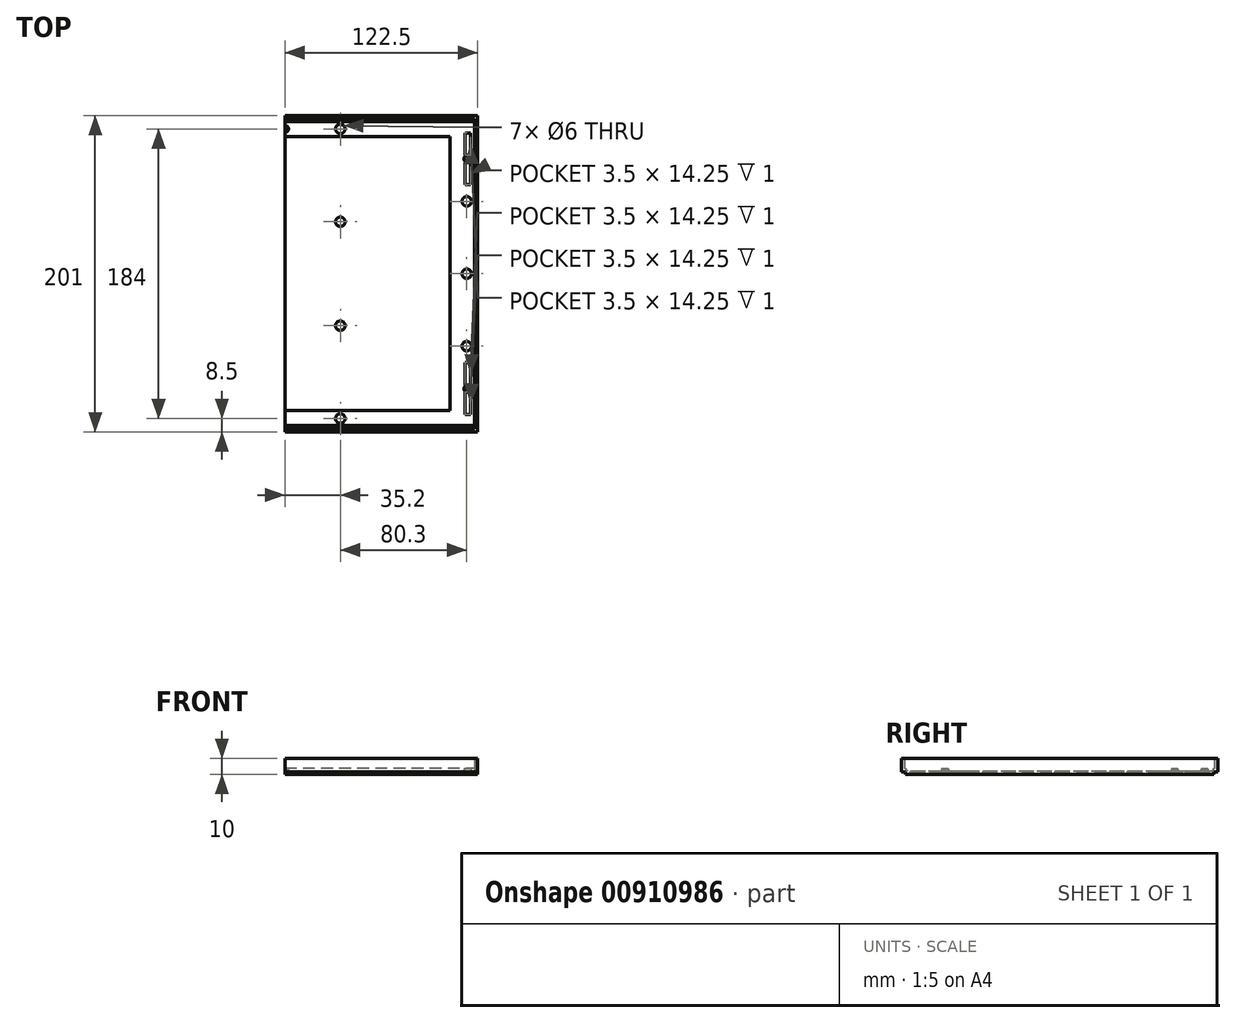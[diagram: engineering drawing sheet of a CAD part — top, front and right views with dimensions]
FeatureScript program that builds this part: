
annotation { "Feature Type Name" : "Feature", "Feature Type Description" : "" }
export const myFeature = defineFeature(function(context is Context, id is Id, definition is map)
    precondition{}
    {
        {
            var Q0;
            Q0=qCreatedBy(makeId("Top.planeOp"),FACE);
            var sketch = newSketch(context, id + "F0", { "sketchPlane" : qUnion([Q0])});
            skLineSegment(sketch, "E0.bottom", {"start": v(0, 0) * mm, "end": v(245, 0) * mm});
            skLineSegment(sketch, "E0.top", {"start": v(0, -201) * mm, "end": v(245, -201) * mm});
            skLineSegment(sketch, "E0.left", {"start": v(0, 0) * mm, "end": v(0, -201) * mm});
            skLineSegment(sketch, "E0.right", {"start": v(245, 0) * mm, "end": v(245, -201) * mm});
            skSolve(sketch);
        }
        {
            var Q0;
            Q0 = qSketchRegion(id + "F0", true);
            extrude(context, id + "F1", {"entities" : qUnion([Q0]), "depth" : 8 * mm, "offsetDistance" : 25 * mm});
        }
        {
            var Q0;
            Q0=makeQuery(id+"F1.opExtrude","CAP_FACE",FACE,{"disambiguationData":[OSD([sQuery(id+"F0.wireOp",EDGE,"E0.bottom"),sQuery(id+"F0.wireOp",EDGE,"E0.top"),sQuery(id+"F0.wireOp",EDGE,"E0.left"),sQuery(id+"F0.wireOp",EDGE,"E0.right")])],"isStart":false});
            shell(context, id + "F2", {"entities" : qUnion([Q0]), "thickness" : 2 * mm});
        }
        {
            var Q0;
            Q0=makeQuery(id+"F2.opShell","OFFSET_FACE",FACE,{"disambiguationData":[OSD([sQuery(id+"F0.wireOp",EDGE,"E0.bottom"),sQuery(id+"F0.wireOp",EDGE,"E0.top"),sQuery(id+"F0.wireOp",EDGE,"E0.left"),sQuery(id+"F0.wireOp",EDGE,"E0.right")])]});
            var sketch = newSketch(context, id + "F3", { "sketchPlane" : qUnion([Q0])});
            skLineSegment(sketch, "E1.bottom", {"start": v(17.5, -13.5) * mm, "end": v(227.5, -13.5) * mm});
            skLineSegment(sketch, "E1.top", {"start": v(17.5, -187.5) * mm, "end": v(227.5, -187.5) * mm});
            skLineSegment(sketch, "E1.left", {"start": v(17.5, -13.5) * mm, "end": v(17.5, -187.5) * mm});
            skLineSegment(sketch, "E1.right", {"start": v(227.5, -13.5) * mm, "end": v(227.5, -187.5) * mm});
            skSolve(sketch);
        }
        {
            var Q0;
            Q0 = qSketchRegion(id + "F3", true);
            extrude(context, id + "F4", {"entities" : qUnion([Q0]), "operationType" : NewBodyOperationType.REMOVE, "oppositeDirection" : true, "depth" : 1 * mm, "offsetDistance" : 25 * mm});
        }
        {
            var Q0;
            Q0=makeQuery(id+"F2.opShell","OFFSET_FACE",FACE,{"disambiguationData":[OSD([sQuery(id+"F0.wireOp",EDGE,"E0.bottom"),sQuery(id+"F0.wireOp",EDGE,"E0.top"),sQuery(id+"F0.wireOp",EDGE,"E0.left"),sQuery(id+"F0.wireOp",EDGE,"E0.right")])]});
            var sketch = newSketch(context, id + "F5", { "sketchPlane" : qUnion([Q0])});
            skLineSegment(sketch, "E2.bottom", {"start": v(4.5, -11) * mm, "end": v(8, -11) * mm});
            skLineSegment(sketch, "E2.top", {"start": v(4.5, -44) * mm, "end": v(8, -44) * mm});
            skLineSegment(sketch, "E2.left", {"start": v(4.5, -11) * mm, "end": v(4.5, -44) * mm});
            skLineSegment(sketch, "E2.right", {"start": v(8, -11) * mm, "end": v(8, -44) * mm});
            skLineSegment(sketch, "E3.bottom", {"start": v(4.5, -157) * mm, "end": v(8, -157) * mm});
            skLineSegment(sketch, "E3.top", {"start": v(4.5, -190) * mm, "end": v(8, -190) * mm});
            skLineSegment(sketch, "E3.left", {"start": v(4.5, -157) * mm, "end": v(4.5, -190) * mm});
            skLineSegment(sketch, "E3.right", {"start": v(8, -157) * mm, "end": v(8, -190) * mm});
            skLineSegment(sketch, "E4.bottom", {"start": v(237, -11) * mm, "end": v(240.5, -11) * mm});
            skLineSegment(sketch, "E4.top", {"start": v(237, -44) * mm, "end": v(240.5, -44) * mm});
            skLineSegment(sketch, "E4.left", {"start": v(237, -11) * mm, "end": v(237, -44) * mm});
            skLineSegment(sketch, "E4.right", {"start": v(240.5, -11) * mm, "end": v(240.5, -44) * mm});
            skLineSegment(sketch, "E5.bottom", {"start": v(237, -157) * mm, "end": v(240.5, -157) * mm});
            skLineSegment(sketch, "E5.top", {"start": v(237, -190) * mm, "end": v(240.5, -190) * mm});
            skLineSegment(sketch, "E5.left", {"start": v(237, -157) * mm, "end": v(237, -190) * mm});
            skLineSegment(sketch, "E5.right", {"start": v(240.5, -157) * mm, "end": v(240.5, -190) * mm});
            skSolve(sketch);
        }
        {
            var Q0;
            Q0 = qSketchRegion(id + "F5", true);
            extrude(context, id + "F6", {"entities" : qUnion([Q0]), "operationType" : NewBodyOperationType.REMOVE, "oppositeDirection" : true, "depth" : 1 * mm, "offsetDistance" : 25 * mm});
        }
        {
            var Q0;
            Q0=makeQuery(id+"F2.opShell","OFFSET_FACE",FACE,{"disambiguationData":[OSD([sQuery(id+"F0.wireOp",EDGE,"E0.bottom"),sQuery(id+"F0.wireOp",EDGE,"E0.top"),sQuery(id+"F0.wireOp",EDGE,"E0.left"),sQuery(id+"F0.wireOp",EDGE,"E0.right")])]});
            var sketch = newSketch(context, id + "F7", { "sketchPlane" : qUnion([Q0])});
            skCircle(sketch, "E6", {"center": v(238, -7) * mm, "radius": 2.75 * mm});
            skCircle(sketch, "E7", {"center": v(7, -7) * mm, "radius": 2.75 * mm});
            skCircle(sketch, "E8", {"center": v(7, -194) * mm, "radius": 2.75 * mm});
            skCircle(sketch, "E9", {"center": v(238, -194) * mm, "radius": 2.75 * mm});
            skSolve(sketch);
        }
        {
            var Q0;
            Q0=makeQuery(id+"F2.opShell","OFFSET_FACE",FACE,{"disambiguationData":[OSD([sQuery(id+"F0.wireOp",EDGE,"E0.bottom"),sQuery(id+"F0.wireOp",EDGE,"E0.top"),sQuery(id+"F0.wireOp",EDGE,"E0.left"),sQuery(id+"F0.wireOp",EDGE,"E0.right")])]});
            var sketch = newSketch(context, id + "F8", { "sketchPlane" : qUnion([Q0])});
            skLineSegment(sketch, "E10", {"start": v(237, -175.75) * mm, "end": v(240.5, -175.75) * mm});
            skLineSegment(sketch, "E11", {"start": v(240.5, -175.75) * mm, "end": v(240.5, -171.25) * mm});
            skLineSegment(sketch, "E12", {"start": v(240.5, -171.25) * mm, "end": v(237, -171.25) * mm});
            skLineSegment(sketch, "E13", {"start": v(237, -175.75) * mm, "end": v(237, -171.25) * mm});
            skLineSegment(sketch, "E14.bottom", {"start": v(240.5, -25.25) * mm, "end": v(237, -25.25) * mm});
            skLineSegment(sketch, "E14.top", {"start": v(240.5, -29.75) * mm, "end": v(237, -29.75) * mm});
            skLineSegment(sketch, "E14.left", {"start": v(240.5, -25.25) * mm, "end": v(240.5, -29.75) * mm});
            skLineSegment(sketch, "E14.right", {"start": v(237, -25.25) * mm, "end": v(237, -29.75) * mm});
            skLineSegment(sketch, "E15.bottom", {"start": v(8, -25.25) * mm, "end": v(4.5, -25.25) * mm});
            skLineSegment(sketch, "E15.top", {"start": v(8, -29.75) * mm, "end": v(4.5, -29.75) * mm});
            skLineSegment(sketch, "E15.left", {"start": v(8, -25.25) * mm, "end": v(8, -29.75) * mm});
            skLineSegment(sketch, "E15.right", {"start": v(4.5, -25.25) * mm, "end": v(4.5, -29.75) * mm});
            skLineSegment(sketch, "E16.bottom", {"start": v(8, -175.75) * mm, "end": v(4.5, -175.75) * mm});
            skLineSegment(sketch, "E16.top", {"start": v(8, -171.25) * mm, "end": v(4.5, -171.25) * mm});
            skLineSegment(sketch, "E16.left", {"start": v(8, -175.75) * mm, "end": v(8, -171.25) * mm});
            skLineSegment(sketch, "E16.right", {"start": v(4.5, -175.75) * mm, "end": v(4.5, -171.25) * mm});
            skSolve(sketch);
        }
        {
            var Q0;
            Q0 = qSketchRegion(id + "F8", true);
            extrude(context, id + "F9", {"entities" : qUnion([Q0]), "operationType" : NewBodyOperationType.ADD, "oppositeDirection" : true, "depth" : 1 * mm, "offsetDistance" : 25 * mm});
        }
        {
            var Q0;
            Q0=makeQuery(id+"F9.boolean.opBoolean","MERGE",FACE,{"derivedFrom":[makeQuery(id+"F2.opShell","OFFSET_FACE",FACE,{"disambiguationData":[OSD([sQuery(id+"F0.wireOp",EDGE,"E0.bottom"),sQuery(id+"F0.wireOp",EDGE,"E0.top"),sQuery(id+"F0.wireOp",EDGE,"E0.left"),sQuery(id+"F0.wireOp",EDGE,"E0.right")])]}),makeQuery(id+"F9.opExtrude","CAP_FACE",FACE,{"disambiguationData":[OSD([sQuery(id+"F8.wireOp",EDGE,"E10"),sQuery(id+"F8.wireOp",EDGE,"E11"),sQuery(id+"F8.wireOp",EDGE,"E12"),sQuery(id+"F8.wireOp",EDGE,"E13")])],"isStart":true}),makeQuery(id+"F9.opExtrude","CAP_FACE",FACE,{"disambiguationData":[OSD([sQuery(id+"F8.wireOp",EDGE,"E14.bottom"),sQuery(id+"F8.wireOp",EDGE,"E14.top"),sQuery(id+"F8.wireOp",EDGE,"E14.left"),sQuery(id+"F8.wireOp",EDGE,"E14.right")])],"isStart":true}),makeQuery(id+"F9.opExtrude","CAP_FACE",FACE,{"disambiguationData":[OSD([sQuery(id+"F8.wireOp",EDGE,"E15.bottom"),sQuery(id+"F8.wireOp",EDGE,"E15.top"),sQuery(id+"F8.wireOp",EDGE,"E15.left"),sQuery(id+"F8.wireOp",EDGE,"E15.right")])],"isStart":true}),makeQuery(id+"F9.opExtrude","CAP_FACE",FACE,{"disambiguationData":[OSD([sQuery(id+"F8.wireOp",EDGE,"E16.bottom"),sQuery(id+"F8.wireOp",EDGE,"E16.top"),sQuery(id+"F8.wireOp",EDGE,"E16.left"),sQuery(id+"F8.wireOp",EDGE,"E16.right")])],"isStart":true})]});
            var sketch = newSketch(context, id + "F10", { "sketchPlane" : qUnion([Q0])});
            skCircle(sketch, "E17", {"center": v(238.5, -27.5) * mm, "radius": 2.25 * mm});
            skCircle(sketch, "E18", {"center": v(6.5, -27.5) * mm, "radius": 2.25 * mm});
            skCircle(sketch, "E19", {"center": v(6.5, -173.5) * mm, "radius": 2.25 * mm});
            skCircle(sketch, "E20", {"center": v(238.5, -173.5) * mm, "radius": 2.25 * mm});
            skCircle(sketch, "E21", {"center": v(122.5, -8.5) * mm, "radius": 2.25 * mm});
            skSolve(sketch);
        }
        {
            var Q0;
            Q0 = qSketchRegion(id + "F10", true);
            extrude(context, id + "F11", {"entities" : qUnion([Q0]), "operationType" : NewBodyOperationType.ADD, "depth" : 1.5 * mm, "offsetDistance" : 25 * mm});
        }
        {
            var Q0;
            Q0=makeQuery(id+"F11.opExtrude","CAP_EDGE",EDGE,{"disambiguationData":[OSD([sQuery(id+"F10.wireOp",EDGE,"E20")])],"isStart":false});
            var Q1;
            Q1=makeQuery(id+"F11.opExtrude","CAP_EDGE",EDGE,{"disambiguationData":[OSD([sQuery(id+"F10.wireOp",EDGE,"E19")])],"isStart":false});
            var Q2;
            Q2=makeQuery(id+"F11.opExtrude","CAP_EDGE",EDGE,{"disambiguationData":[OSD([sQuery(id+"F10.wireOp",EDGE,"E17")])],"isStart":false});
            var Q3;
            Q3=makeQuery(id+"F11.opExtrude","CAP_EDGE",EDGE,{"disambiguationData":[OSD([sQuery(id+"F10.wireOp",EDGE,"E18")])],"isStart":false});
            var Q4;
            Q4=makeQuery(id+"F11.opExtrude","CAP_EDGE",EDGE,{"disambiguationData":[OSD([sQuery(id+"F10.wireOp",EDGE,"E21")])],"isStart":false});
            chamfer(context, id + "F12", {"entities" : qUnion([Q0, Q1, Q2, Q3, Q4]), "chamferType" : ChamferType.OFFSET_ANGLE, "width" : .15 * mm, "oppositeDirection" : false, "angle" : 84.25 * degree, "tangentPropagation" : true});
        }
        {
            var Q0;
            Q0=makeQuery(id+"F9.boolean.opBoolean","MERGE",FACE,{"derivedFrom":[makeQuery(id+"F2.opShell","OFFSET_FACE",FACE,{"disambiguationData":[OSD([sQuery(id+"F0.wireOp",EDGE,"E0.bottom"),sQuery(id+"F0.wireOp",EDGE,"E0.top"),sQuery(id+"F0.wireOp",EDGE,"E0.left"),sQuery(id+"F0.wireOp",EDGE,"E0.right")])]}),makeQuery(id+"F9.opExtrude","CAP_FACE",FACE,{"disambiguationData":[OSD([sQuery(id+"F8.wireOp",EDGE,"E10"),sQuery(id+"F8.wireOp",EDGE,"E11"),sQuery(id+"F8.wireOp",EDGE,"E12"),sQuery(id+"F8.wireOp",EDGE,"E13")])],"isStart":true}),makeQuery(id+"F9.opExtrude","CAP_FACE",FACE,{"disambiguationData":[OSD([sQuery(id+"F8.wireOp",EDGE,"E14.bottom"),sQuery(id+"F8.wireOp",EDGE,"E14.top"),sQuery(id+"F8.wireOp",EDGE,"E14.left"),sQuery(id+"F8.wireOp",EDGE,"E14.right")])],"isStart":true}),makeQuery(id+"F9.opExtrude","CAP_FACE",FACE,{"disambiguationData":[OSD([sQuery(id+"F8.wireOp",EDGE,"E15.bottom"),sQuery(id+"F8.wireOp",EDGE,"E15.top"),sQuery(id+"F8.wireOp",EDGE,"E15.left"),sQuery(id+"F8.wireOp",EDGE,"E15.right")])],"isStart":true}),makeQuery(id+"F9.opExtrude","CAP_FACE",FACE,{"disambiguationData":[OSD([sQuery(id+"F8.wireOp",EDGE,"E16.bottom"),sQuery(id+"F8.wireOp",EDGE,"E16.top"),sQuery(id+"F8.wireOp",EDGE,"E16.left"),sQuery(id+"F8.wireOp",EDGE,"E16.right")])],"isStart":true})]});
            var sketch = newSketch(context, id + "F13", { "sketchPlane" : qUnion([Q0])});
            skCircle(sketch, "E22", {"center": v(7, -54.5) * mm, "radius": 3 * mm});
            skCircle(sketch, "E23", {"center": v(7, -100.5) * mm, "radius": 3 * mm});
            skCircle(sketch, "E24", {"center": v(7, -146.5) * mm, "radius": 3 * mm});
            skCircle(sketch, "E25.MirrorC", {"center": v(238, -54.5) * mm, "radius": 3 * mm});
            skCircle(sketch, "E26.MirrorC", {"center": v(238, -100.5) * mm, "radius": 3 * mm});
            skCircle(sketch, "E27.MirrorC", {"center": v(238, -146.5) * mm, "radius": 3 * mm});
            skCircle(sketch, "E28", {"center": v(87.3, -8.5) * mm, "radius": 3 * mm});
            skCircle(sketch, "E29", {"center": v(87.3, -67.5) * mm, "radius": 3 * mm});
            skPoint(sketch, "E30.0", {"position": v(122.5, -12.5) * mm});
            skPoint(sketch, "E31.MirrorP", {"position": v(122.5, -364.5) * mm});
            skPoint(sketch, "E32.MirrorP", {"position": v(122.5, -188.5) * mm});
            skCircle(sketch, "E33.MirrorC", {"center": v(157.7, -8.5) * mm, "radius": 3 * mm});
            skCircle(sketch, "E34.MirrorC", {"center": v(157.7, -67.5) * mm, "radius": 3 * mm});
            skCircle(sketch, "E35.MirrorC", {"center": v(157.7, -133.5) * mm, "radius": 3 * mm});
            skCircle(sketch, "E36.MirrorC", {"center": v(157.7, -192.5) * mm, "radius": 3 * mm});
            skCircle(sketch, "E37.MirrorC", {"center": v(87.3, -192.5) * mm, "radius": 3 * mm});
            skCircle(sketch, "E38.MirrorC", {"center": v(87.3, -133.5) * mm, "radius": 3 * mm});
            skSolve(sketch);
        }
        {
            var Q0;
            Q0 = qSketchRegion(id + "F13", true);
            extrude(context, id + "F14", {"entities" : qUnion([Q0]), "operationType" : NewBodyOperationType.REMOVE, "endBound" : BoundingType.THROUGH_ALL, "oppositeDirection" : true, "depth" : 25 * mm, "offsetDistance" : 25 * mm});
        }
        {
            var Q0;
            Q0=makeQuery(id+"F1.opExtrude","SWEPT_FACE",FACE,{"disambiguationData":[OSD([sQuery(id+"F0.wireOp",EDGE,"E0.left")])]});
            var sketch = newSketch(context, id + "F15", { "sketchPlane" : qUnion([Q0])});
            skLineSegment(sketch, "E39.bottom", {"start": v(2.5, 0) * mm, "end": v(0, 0) * mm});
            skLineSegment(sketch, "E39.top", {"start": v(2.5, 1.5) * mm, "end": v(0, 1.5) * mm});
            skLineSegment(sketch, "E39.left", {"start": v(2.5, 0) * mm, "end": v(2.5, 1.5) * mm});
            skLineSegment(sketch, "E39.right", {"start": v(0, 0) * mm, "end": v(0, 1.5) * mm});
            skPoint(sketch, "E40.oppositeSnap0", {"position": v(1.25, 1.5) * mm});
            skLineSegment(sketch, "E40.bottom", {"start": v(198.5, 0) * mm, "end": v(201, 0) * mm});
            skLineSegment(sketch, "E40.top", {"start": v(198.5, 1.5) * mm, "end": v(201, 1.5) * mm});
            skLineSegment(sketch, "E40.left", {"start": v(198.5, 0) * mm, "end": v(198.5, 1.5) * mm});
            skLineSegment(sketch, "E40.right", {"start": v(201, 0) * mm, "end": v(201, 1.5) * mm});
            skSolve(sketch);
        }
        {
            var Q0;
            Q0 = qSketchRegion(id + "F15", true);
            extrude(context, id + "F16", {"entities" : qUnion([Q0]), "operationType" : NewBodyOperationType.REMOVE, "endBound" : BoundingType.THROUGH_ALL, "oppositeDirection" : true, "depth" : 25 * mm, "offsetDistance" : 25 * mm});
        }
        {
            var Q0;
            {var subQ0=sQuery(id+"F0.wireOp",EDGE,"E0.bottom");Q0=makeQuery(id+"F2.opShell","OFFSET_EDGE",EDGE,{"disambiguationData":[OSD([subQ0]),TDD([makeQuery(id+"F1.opExtrude","CAP_EDGE",EDGE,{"disambiguationData":[OSD([subQ0])],"isStart":true})])]});}
            var Q1;
            {var subQ0=sQuery(id+"F0.wireOp",EDGE,"E0.top");Q1=makeQuery(id+"F2.opShell","OFFSET_EDGE",EDGE,{"disambiguationData":[OSD([subQ0]),TDD([makeQuery(id+"F1.opExtrude","CAP_EDGE",EDGE,{"disambiguationData":[OSD([subQ0])],"isStart":true})])]});}
            chamfer(context, id + "F17", {"entities" : qUnion([Q0, Q1]), "width" : 2 * mm, "tangentPropagation" : true});
        }
        {
            var Q0;
            Q0=makeQuery(id+"F1.opExtrude","CAP_FACE",FACE,{"disambiguationData":[OSD([sQuery(id+"F0.wireOp",EDGE,"E0.bottom"),sQuery(id+"F0.wireOp",EDGE,"E0.top"),sQuery(id+"F0.wireOp",EDGE,"E0.left"),sQuery(id+"F0.wireOp",EDGE,"E0.right")])],"isStart":false});
            extrude(context, id + "F18", {"entities" : qUnion([Q0]), "operationType" : NewBodyOperationType.ADD, "depth" : 2 * mm, "offsetDistance" : 25 * mm});
        }
        {
            var Q0;
            Q0=makeQuery(id+"F18.opExtrude","CAP_FACE",FACE,{"disambiguationData":[OSD([sQuery(id+"F0.wireOp",EDGE,"E0.bottom"),sQuery(id+"F0.wireOp",EDGE,"E0.top"),sQuery(id+"F0.wireOp",EDGE,"E0.left"),sQuery(id+"F0.wireOp",EDGE,"E0.right")])],"isStart":false});
            var sketch = newSketch(context, id + "F19", { "sketchPlane" : qUnion([Q0])});
            skPoint(sketch, "E41.firstSnap0", {"position": v(122.5, 0) * mm});
            skLineSegment(sketch, "E41.bottom", {"start": v(122.5, 4.6) * mm, "end": v(-19.44, 4.6) * mm});
            skLineSegment(sketch, "E41.top", {"start": v(122.5, -215.35) * mm, "end": v(-19.44, -215.35) * mm});
            skLineSegment(sketch, "E41.left", {"start": v(122.5, 4.6) * mm, "end": v(122.5, -215.35) * mm});
            skLineSegment(sketch, "E41.right", {"start": v(-19.44, 4.6) * mm, "end": v(-19.44, -215.35) * mm});
            skSolve(sketch);
        }
        {
            var Q0;
            Q0 = qSketchRegion(id + "F19", true);
            extrude(context, id + "F20", {"entities" : qUnion([Q0]), "operationType" : NewBodyOperationType.REMOVE, "endBound" : BoundingType.THROUGH_ALL, "oppositeDirection" : true, "depth" : 25 * mm, "offsetDistance" : 25 * mm});
        }
    });
